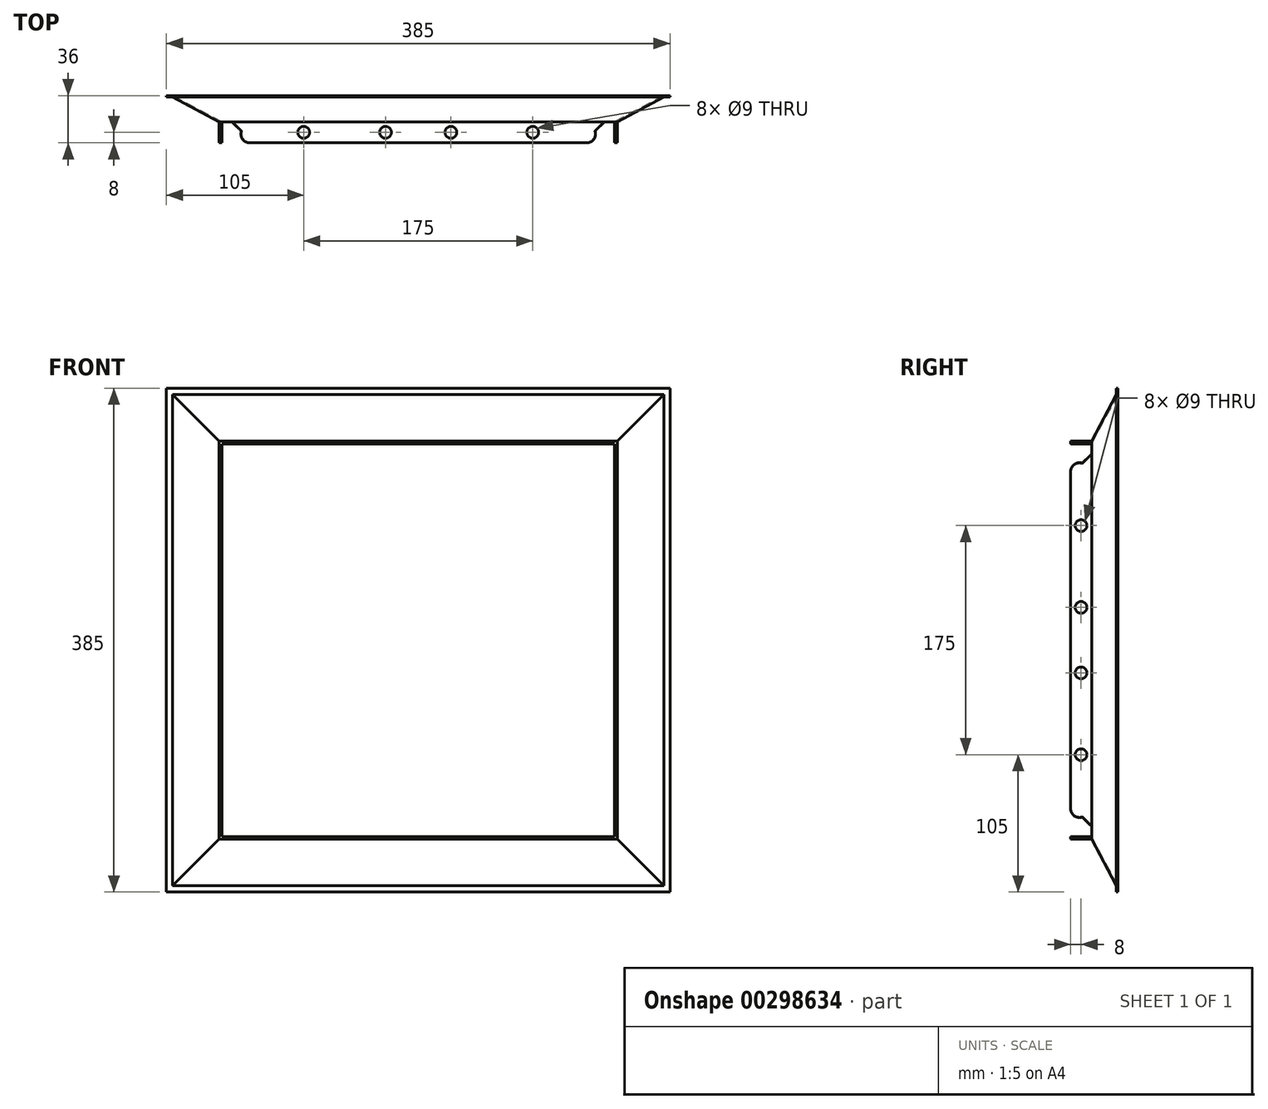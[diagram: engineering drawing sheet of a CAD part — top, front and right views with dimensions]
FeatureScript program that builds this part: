
annotation { "Feature Type Name" : "Feature", "Feature Type Description" : "" }
export const myFeature = defineFeature(function(context is Context, id is Id, definition is map)
    precondition{}
    {
        {
            var Q0;
            Q0=qCreatedBy(makeId("Front.planeOp"),FACE);
            var sketch = newSketch(context, id + "F0", { "sketchPlane" : qUnion([Q0])});
            skLineSegment(sketch, "E0.bottom", {"start": v(-192.5, 192.5) * mm, "end": v(192.5, 192.5) * mm});
            skLineSegment(sketch, "E0.top", {"start": v(-192.5, -192.5) * mm, "end": v(192.5, -192.5) * mm});
            skLineSegment(sketch, "E0.left", {"start": v(-192.5, 192.5) * mm, "end": v(-192.5, -192.5) * mm});
            skLineSegment(sketch, "E0.right", {"start": v(192.5, 192.5) * mm, "end": v(192.5, -192.5) * mm});
            skLineSegment(sketch, "E1.bottom", {"start": v(187.5, -187.5) * mm, "end": v(-187.5, -187.5) * mm});
            skLineSegment(sketch, "E1.top", {"start": v(187.5, 187.5) * mm, "end": v(-187.5, 187.5) * mm});
            skLineSegment(sketch, "E1.left", {"start": v(187.5, -187.5) * mm, "end": v(187.5, 187.5) * mm});
            skLineSegment(sketch, "E1.right", {"start": v(-187.5, -187.5) * mm, "end": v(-187.5, 187.5) * mm});
            skPoint(sketch, "E1.middle", {"position": v(0, 0) * mm});
            skPoint(sketch, "E2.endSnap0", {"position": v(-187.5, 0) * mm});
            skSolve(sketch);
        }
        {
            var Q0;
            Q0=makeQuery(id+"F0.imprint","IMPRINT",FACE,{"disambiguationData":[TD([[makeQuery(id+"F0.imprint","IMPRINT",EDGE,{"derivedFrom":sQuery(id+"F0.wireOp",EDGE,"E0.bottom")}),-1.0]])]});
            cPlane(context, id + "F1", {"entities" : qUnion([Q0]), "cplaneType" : CPlaneType.OFFSET, "offset" : 20 * mm, "width" : 150 * mm, "height" : 150 * mm});
        }
        {
            var Q0;
            Q0=qCreatedBy(id+"F1.planeOp",FACE);
            var sketch = newSketch(context, id + "F2", { "sketchPlane" : qUnion([Q0])});
            skLineSegment(sketch, "E3.bottom", {"start": v(150, -150) * mm, "end": v(-150, -150) * mm});
            skLineSegment(sketch, "E3.top", {"start": v(150, 150) * mm, "end": v(-150, 150) * mm});
            skLineSegment(sketch, "E3.left", {"start": v(150, -150) * mm, "end": v(150, 150) * mm});
            skLineSegment(sketch, "E3.right", {"start": v(-150, -150) * mm, "end": v(-150, 150) * mm});
            skPoint(sketch, "E3.middle", {"position": v(0, 0) * mm});
            skSolve(sketch);
        }
        {
            var Q0;
            Q0=makeQuery(id+"F0.imprint","IMPRINT",FACE,{"disambiguationData":[TD([[makeQuery(id+"F0.imprint","IMPRINT",EDGE,{"derivedFrom":sQuery(id+"F0.wireOp",EDGE,"E1.bottom")}),-1.0]])]});
            var Q1;
            Q1=makeQuery(id+"F2.imprint","IMPRINT",FACE,{"disambiguationData":[TD([[makeQuery(id+"F2.imprint","IMPRINT",EDGE,{"derivedFrom":sQuery(id+"F2.wireOp",EDGE,"E3.bottom")}),-1.0]])]});
            loft(context, id + "F3", {"sheetProfilesArray" : [{ "sheetProfileEntities" : qUnion([Q0]) }, { "sheetProfileEntities" : qUnion([Q1]) }]});
        }
        {
            var Q0;
            Q0=makeQuery(id+"F3.opLoft","CAP_FACE",FACE,{"disambiguationData":[OSD([makeQuery(id+"F2.imprint","IMPRINT",FACE,{"disambiguationData":[TD([[makeQuery(id+"F2.imprint","IMPRINT",EDGE,{"derivedFrom":sQuery(id+"F2.wireOp",EDGE,"E3.bottom")}),-1.0]])]})])],"isStart":true});
            var Q1;
            Q1=makeQuery(id+"F3.opLoft","CAP_FACE",FACE,{"disambiguationData":[OSD([makeQuery(id+"F0.imprint","IMPRINT",FACE,{"disambiguationData":[TD([[makeQuery(id+"F0.imprint","IMPRINT",EDGE,{"derivedFrom":sQuery(id+"F0.wireOp",EDGE,"E1.bottom")}),-1.0]])]})])],"isStart":true});
            shell(context, id + "F4", {"entities" : qUnion([Q0, Q1]), "thickness" : 1 * mm, "oppositeDirection" : true});
        }
        {
            var Q0;
            Q0=makeQuery(id+"F0.imprint","IMPRINT",FACE,{"disambiguationData":[TD([[makeQuery(id+"F0.imprint","IMPRINT",EDGE,{"derivedFrom":sQuery(id+"F0.wireOp",EDGE,"E0.bottom")}),-1.0]])]});
            extrude(context, id + "F5", {"entities" : qUnion([Q0]), "operationType" : NewBodyOperationType.ADD, "depth" : 1 * mm});
        }
        {
            var Q0;
            Q0=makeQuery(id+"F3.opLoft","CAP_FACE",FACE,{"disambiguationData":[OSD([makeQuery(id+"F2.imprint","IMPRINT",FACE,{"disambiguationData":[TD([[makeQuery(id+"F2.imprint","IMPRINT",EDGE,{"derivedFrom":sQuery(id+"F2.wireOp",EDGE,"E3.bottom")}),-1.0]])]})])],"isStart":true});
            var sketch = newSketch(context, id + "F6", { "sketchPlane" : qUnion([Q0])});
            skLineSegment(sketch, "E4.0", {"start": v(-150, -150) * mm, "end": v(150, -150) * mm});
            skLineSegment(sketch, "E5.0", {"start": v(150, -150) * mm, "end": v(150, 150) * mm});
            skLineSegment(sketch, "E6.0", {"start": v(152.12, -152.12) * mm, "end": v(152.12, 152.12) * mm});
            skLineSegment(sketch, "E7.0", {"start": v(152.12, 152.13) * mm, "end": v(-152.12, 152.12) * mm});
            skLineSegment(sketch, "E8.0", {"start": v(150, 150) * mm, "end": v(-150, 150) * mm});
            skLineSegment(sketch, "E9.0", {"start": v(-152.12, 152.12) * mm, "end": v(-152.12, -152.12) * mm});
            skLineSegment(sketch, "E10.0", {"start": v(-150, 150) * mm, "end": v(-150, -150) * mm});
            skLineSegment(sketch, "E11.0", {"start": v(-152.12, -152.12) * mm, "end": v(152.12, -152.12) * mm});
            skSolve(sketch);
        }
        {
            var Q0;
            Q0=qSketchRegion(id+"F6",true);
            extrude(context, id + "F7", {"entities" : qUnion([Q0]), "operationType" : NewBodyOperationType.ADD, "depth" : 16 * mm});
        }
        {
            var Q0;
            Q0=makeQuery(id+"F7.opExtrude","SWEPT_FACE",FACE,{"disambiguationData":[OSD([sQuery(id+"F6.wireOp",EDGE,"E7.0")])]});
            var sketch = newSketch(context, id + "F8", { "sketchPlane" : qUnion([Q0])});
            skLineSegment(sketch, "E12", {"start": v(152.12, -20) * mm, "end": v(142.12, -20) * mm});
            skLineSegment(sketch, "E13", {"start": v(142.12, -20) * mm, "end": v(135.05, -27.07) * mm});
            skArc(sketch, "E14", {"start": v(128.74, -36) * mm, "mid": v(134.2, -33.17) * mm, "end": v(135.05, -27.07) * mm});
            skLineSegment(sketch, "E15", {"start": v(152.12, -20) * mm, "end": v(152.12, -36) * mm});
            skLineSegment(sketch, "E16", {"start": v(128.74, -36) * mm, "end": v(152.12, -36) * mm});
            skLineSegment(sketch, "E17", {"start": v(-152.12, -20) * mm, "end": v(-142.12, -20) * mm});
            skLineSegment(sketch, "E18", {"start": v(-142.12, -20) * mm, "end": v(-135.05, -27.07) * mm});
            skArc(sketch, "E19", {"start": v(-135.05, -27.07) * mm, "mid": v(-134.2, -33.17) * mm, "end": v(-128.74, -36) * mm});
            skLineSegment(sketch, "E20", {"start": v(-128.74, -36) * mm, "end": v(-152.12, -36) * mm});
            skLineSegment(sketch, "E21", {"start": v(-152.12, -36) * mm, "end": v(-152.12, -20) * mm});
            skSolve(sketch);
        }
        {
            var Q0;
            Q0=makeQuery(id+"F8.imprint","IMPRINT",FACE,{"disambiguationData":[TD([[makeQuery(id+"F8.imprint","IMPRINT",EDGE,{"derivedFrom":sQuery(id+"F8.wireOp",EDGE,"E12")}),1.0]])]});
            var Q1;
            Q1=sQuery(id+"F8.wireOp",EDGE,"E15");
            revolve(context, id + "F9", {"operationType" : NewBodyOperationType.REMOVE, "entities" : qUnion([Q0]), "axis" : qUnion([Q1]), "revolveType" : RevolveType.FULL, "oppositeDirection" : true});
        }
        {
            var Q0;
            Q0=makeQuery(id+"F8.imprint","IMPRINT",FACE,{"disambiguationData":[TD([[makeQuery(id+"F8.imprint","IMPRINT",EDGE,{"derivedFrom":sQuery(id+"F8.wireOp",EDGE,"E17")}),1.0]])]});
            var Q1;
            Q1=sQuery(id+"F8.wireOp",EDGE,"E21");
            revolve(context, id + "F10", {"operationType" : NewBodyOperationType.REMOVE, "entities" : qUnion([Q0]), "axis" : qUnion([Q1]), "revolveType" : RevolveType.FULL, "oppositeDirection" : true});
        }
        {
            var Q0;
            Q0=makeQuery(id+"F7.opExtrude","SWEPT_FACE",FACE,{"disambiguationData":[OSD([sQuery(id+"F6.wireOp",EDGE,"E11.0")])]});
            var sketch = newSketch(context, id + "F11", { "sketchPlane" : qUnion([Q0])});
            skLineSegment(sketch, "E22.0", {"start": v(-128.74, 36) * mm, "end": v(-152.12, 36) * mm});
            skArc(sketch, "E23.0", {"start": v(-135.05, 27.07) * mm, "mid": v(-134.2, 33.17) * mm, "end": v(-128.74, 36) * mm});
            skLineSegment(sketch, "E23.1", {"start": v(-152.12, 36) * mm, "end": v(-152.12, 20) * mm});
            skLineSegment(sketch, "E23.2", {"start": v(-142.12, 20) * mm, "end": v(-135.05, 27.07) * mm});
            skLineSegment(sketch, "E24.0", {"start": v(-152.12, 20) * mm, "end": v(-142.12, 20) * mm});
            skLineSegment(sketch, "E25.0", {"start": v(128.74, 36) * mm, "end": v(152.12, 36) * mm});
            skLineSegment(sketch, "E26.0", {"start": v(152.12, 20) * mm, "end": v(152.12, 36) * mm});
            skArc(sketch, "E27.0", {"start": v(128.74, 36) * mm, "mid": v(134.2, 33.17) * mm, "end": v(135.05, 27.07) * mm});
            skLineSegment(sketch, "E28.0", {"start": v(142.12, 20) * mm, "end": v(135.05, 27.07) * mm});
            skLineSegment(sketch, "E29.0", {"start": v(152.12, 20) * mm, "end": v(142.12, 20) * mm});
            skSolve(sketch);
        }
        {
            var Q0;
            Q0=makeQuery(id+"F11.imprint","IMPRINT",FACE,{"disambiguationData":[TD([[makeQuery(id+"F11.imprint","IMPRINT",EDGE,{"derivedFrom":sQuery(id+"F11.wireOp",EDGE,"E25.0")}),-1.0]])]});
            var Q1;
            Q1=sQuery(id+"F11.wireOp",EDGE,"E26.0");
            revolve(context, id + "F12", {"operationType" : NewBodyOperationType.REMOVE, "entities" : qUnion([Q0]), "axis" : qUnion([Q1]), "revolveType" : RevolveType.FULL, "oppositeDirection" : true});
        }
        {
            var Q0;
            Q0=makeQuery(id+"F11.imprint","IMPRINT",FACE,{"disambiguationData":[TD([[makeQuery(id+"F11.imprint","IMPRINT",EDGE,{"derivedFrom":sQuery(id+"F11.wireOp",EDGE,"E22.0")}),-1.0]])]});
            var Q1;
            Q1=sQuery(id+"F11.wireOp",EDGE,"E23.1");
            revolve(context, id + "F13", {"operationType" : NewBodyOperationType.REMOVE, "entities" : qUnion([Q0]), "axis" : qUnion([Q1]), "revolveType" : RevolveType.FULL, "oppositeDirection" : true});
        }
        {
            var Q0;
            Q0=makeQuery(id+"F7.opExtrude","SWEPT_FACE",FACE,{"disambiguationData":[OSD([sQuery(id+"F6.wireOp",EDGE,"E11.0")])]});
            var sketch = newSketch(context, id + "F14", { "sketchPlane" : qUnion([Q0])});
            skLineSegment(sketch, "E30", {"start": v(-224.61, 28) * mm, "end": v(231.22, 28) * mm, "construction": true});
            skCircle(sketch, "E31", {"center": v(-87.5, 28) * mm, "radius": 4.5 * mm});
            skCircle(sketch, "E32", {"center": v(-25, 28) * mm, "radius": 4.5 * mm});
            skCircle(sketch, "E33", {"center": v(25, 28) * mm, "radius": 4.5 * mm});
            skCircle(sketch, "E34", {"center": v(87.5, 28) * mm, "radius": 4.5 * mm});
            skSolve(sketch);
        }
        {
            var Q0;
            Q0=makeQuery(id+"F14.imprint","IMPRINT",FACE,{"disambiguationData":[TD([[makeQuery(id+"F14.imprint","IMPRINT",EDGE,{"derivedFrom":sQuery(id+"F14.wireOp",EDGE,"E31")}),1.0]])]});
            var Q1;
            Q1=makeQuery(id+"F14.imprint","IMPRINT",FACE,{"disambiguationData":[TD([[makeQuery(id+"F14.imprint","IMPRINT",EDGE,{"derivedFrom":sQuery(id+"F14.wireOp",EDGE,"E32")}),1.0]])]});
            var Q2;
            Q2=makeQuery(id+"F14.imprint","IMPRINT",FACE,{"disambiguationData":[TD([[makeQuery(id+"F14.imprint","IMPRINT",EDGE,{"derivedFrom":sQuery(id+"F14.wireOp",EDGE,"E33")}),1.0]])]});
            var Q3;
            Q3=makeQuery(id+"F14.imprint","IMPRINT",FACE,{"disambiguationData":[TD([[makeQuery(id+"F14.imprint","IMPRINT",EDGE,{"derivedFrom":sQuery(id+"F14.wireOp",EDGE,"E34")}),1.0]])]});
            extrude(context, id + "F15", {"entities" : qUnion([Q0, Q1, Q2, Q3]), "operationType" : NewBodyOperationType.REMOVE, "endBound" : BoundingType.THROUGH_ALL, "oppositeDirection" : true, "depth" : 25 * mm});
        }
        {
            var Q0;
            Q0=makeQuery(id+"F7.opExtrude","SWEPT_FACE",FACE,{"disambiguationData":[OSD([sQuery(id+"F6.wireOp",EDGE,"E6.0")])]});
            var sketch = newSketch(context, id + "F16", { "sketchPlane" : qUnion([Q0])});
            skLineSegment(sketch, "E35", {"start": v(-28, -170.73) * mm, "end": v(-28, 196.38) * mm, "construction": true});
            skCircle(sketch, "E36", {"center": v(-28, -87.5) * mm, "radius": 4.5 * mm});
            skCircle(sketch, "E37", {"center": v(-28, -25) * mm, "radius": 4.5 * mm});
            skCircle(sketch, "E38", {"center": v(-28, 25) * mm, "radius": 4.5 * mm});
            skCircle(sketch, "E39", {"center": v(-28, 87.5) * mm, "radius": 4.5 * mm});
            skSolve(sketch);
        }
        {
            var Q0;
            Q0=makeQuery(id+"F16.imprint","IMPRINT",FACE,{"disambiguationData":[TD([[makeQuery(id+"F16.imprint","IMPRINT",EDGE,{"derivedFrom":sQuery(id+"F16.wireOp",EDGE,"E36")}),1.0]])]});
            var Q1;
            Q1=makeQuery(id+"F16.imprint","IMPRINT",FACE,{"disambiguationData":[TD([[makeQuery(id+"F16.imprint","IMPRINT",EDGE,{"derivedFrom":sQuery(id+"F16.wireOp",EDGE,"E37")}),1.0]])]});
            var Q2;
            Q2=makeQuery(id+"F16.imprint","IMPRINT",FACE,{"disambiguationData":[TD([[makeQuery(id+"F16.imprint","IMPRINT",EDGE,{"derivedFrom":sQuery(id+"F16.wireOp",EDGE,"E38")}),1.0]])]});
            var Q3;
            Q3=makeQuery(id+"F16.imprint","IMPRINT",FACE,{"disambiguationData":[TD([[makeQuery(id+"F16.imprint","IMPRINT",EDGE,{"derivedFrom":sQuery(id+"F16.wireOp",EDGE,"E39")}),1.0]])]});
            extrude(context, id + "F17", {"entities" : qUnion([Q0, Q1, Q2, Q3]), "operationType" : NewBodyOperationType.REMOVE, "endBound" : BoundingType.THROUGH_ALL, "oppositeDirection" : true, "depth" : 25 * mm});
        }
    });
